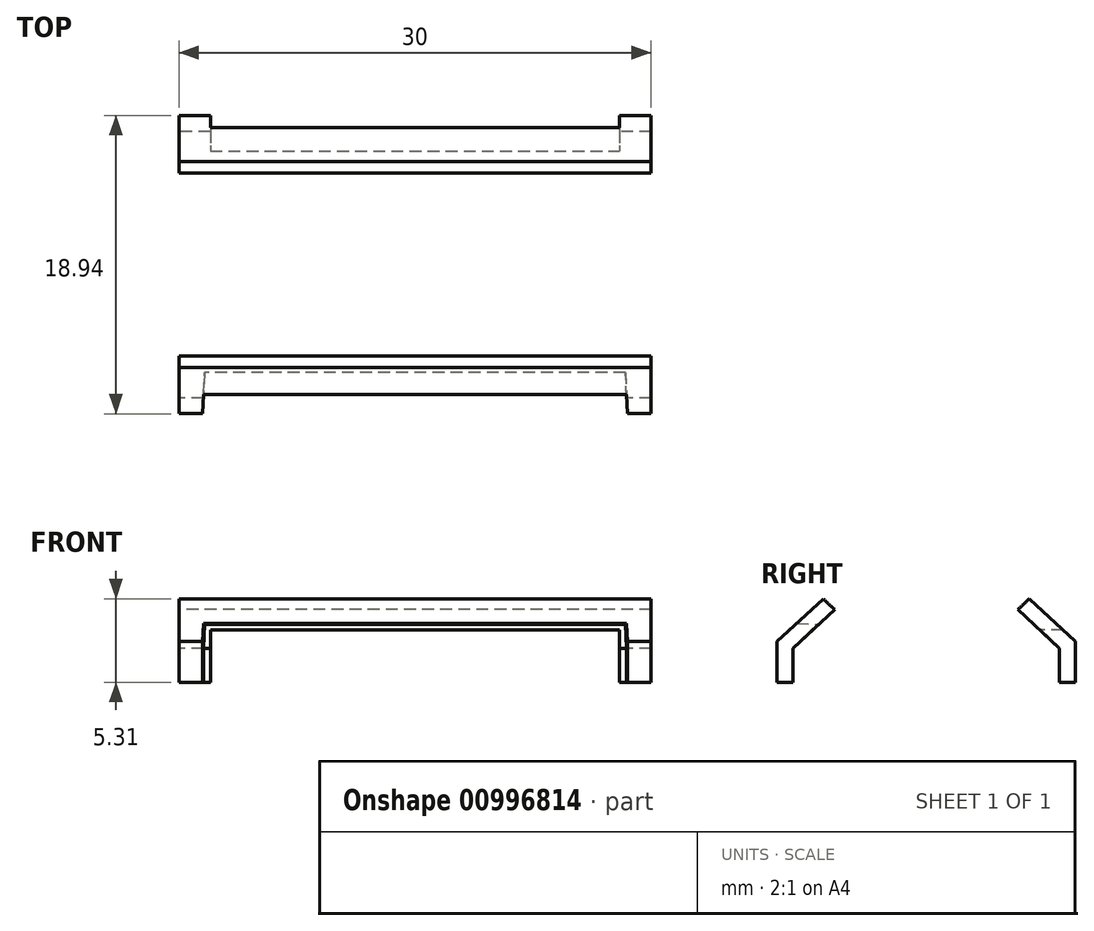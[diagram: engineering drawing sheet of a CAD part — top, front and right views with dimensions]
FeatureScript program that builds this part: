
annotation { "Feature Type Name" : "Feature", "Feature Type Description" : "" }
export const myFeature = defineFeature(function(context is Context, id is Id, definition is map)
    precondition{}
    {
        {
            var Q0;
            Q0=qCreatedBy(makeId("Right.planeOp"),FACE);
            var sketch = newSketch(context, id + "F0", { "sketchPlane" : qUnion([Q0])});
            skArc(sketch, "E0", {"start": v(5.8, -6.88) * mm, "mid": v(6.18, -6.54) * mm, "end": v(6.54, -6.19) * mm});
            skLineSegment(sketch, "E1", {"start": v(6.54, -6.19) * mm, "end": v(9.47, -8.9) * mm});
            skLineSegment(sketch, "E2", {"start": v(9.47, -8.9) * mm, "end": v(9.47, -11.5) * mm});
            skLineSegment(sketch, "E3", {"start": v(9.47, -11.5) * mm, "end": v(8.47, -11.5) * mm});
            skLineSegment(sketch, "E4", {"start": v(8.47, -11.5) * mm, "end": v(8.47, -9.33) * mm});
            skLineSegment(sketch, "E5", {"start": v(8.47, -9.33) * mm, "end": v(5.8, -6.88) * mm});
            skLineSegment(sketch, "E6.MirrorCS", {"start": v(-6.54, -6.19) * mm, "end": v(-9.47, -8.9) * mm});
            skArc(sketch, "E7.MirrorCS", {"start": v(-5.8, -6.88) * mm, "mid": v(-6.18, -6.54) * mm, "end": v(-6.54, -6.19) * mm});
            skLineSegment(sketch, "E8.MirrorCS", {"start": v(-8.47, -9.33) * mm, "end": v(-5.8, -6.88) * mm});
            skLineSegment(sketch, "E9.MirrorCS", {"start": v(-8.47, -11.5) * mm, "end": v(-8.47, -9.33) * mm});
            skLineSegment(sketch, "E10.MirrorCS", {"start": v(-9.47, -8.9) * mm, "end": v(-9.47, -11.5) * mm});
            skLineSegment(sketch, "E11.MirrorCS", {"start": v(-9.47, -11.5) * mm, "end": v(-8.47, -11.5) * mm});
            skPoint(sketch, "E12.start.orphan", {"position": v(0, 6.68) * mm});
            skSolve(sketch);
        }
        {
            var Q0;
            Q0=makeQuery(id+"F0.imprint","IMPRINT",FACE,{"disambiguationData":[TD([[makeQuery(id+"F0.imprint","IMPRINT",EDGE,{"derivedFrom":sQuery(id+"F0.wireOp",EDGE,"E0")}),-1.0]])]});
            var Q1;
            Q1=makeQuery(id+"F0.imprint","IMPRINT",FACE,{"disambiguationData":[TD([[makeQuery(id+"F0.imprint","IMPRINT",EDGE,{"derivedFrom":sQuery(id+"F0.wireOp",EDGE,"E6.MirrorCS")}),1.0]])]});
            extrude(context, id + "F1", {"entities" : qUnion([Q0, Q1]), "depth" : 30 * mm, "offsetDistance" : 25 * mm});
        }
        {
            var Q0;
            Q0=qCreatedBy(makeId("Front.planeOp"),FACE);
            var sketch = newSketch(context, id + "F2", { "sketchPlane" : qUnion([Q0])});
            skLineSegment(sketch, "E13.bottom", {"start": v(2, -13.19) * mm, "end": v(28, -13.19) * mm});
            skLineSegment(sketch, "E13.top", {"start": v(2, -8.19) * mm, "end": v(28, -8.19) * mm});
            skLineSegment(sketch, "E13.left", {"start": v(2, -13.19) * mm, "end": v(2, -8.19) * mm});
            skLineSegment(sketch, "E13.right", {"start": v(28, -13.19) * mm, "end": v(28, -8.19) * mm});
            skSolve(sketch);
        }
        {
            var Q0;
            Q0 = qSketchRegion(id + "F2", true);
            extrude(context, id + "F3", {"entities" : qUnion([Q0]), "operationType" : NewBodyOperationType.REMOVE, "depth" : 25 * mm, "offsetDistance" : 25 * mm, "hasDraft" : true, "draftAngle" : 3 * degree});
        }
        {
            var Q0;
            Q0 = qSketchRegion(id + "F2", true);
            extrude(context, id + "F4", {"entities" : qUnion([Q0]), "operationType" : NewBodyOperationType.REMOVE, "oppositeDirection" : true, "depth" : 25 * mm, "offsetDistance" : 25 * mm});
        }
    });
